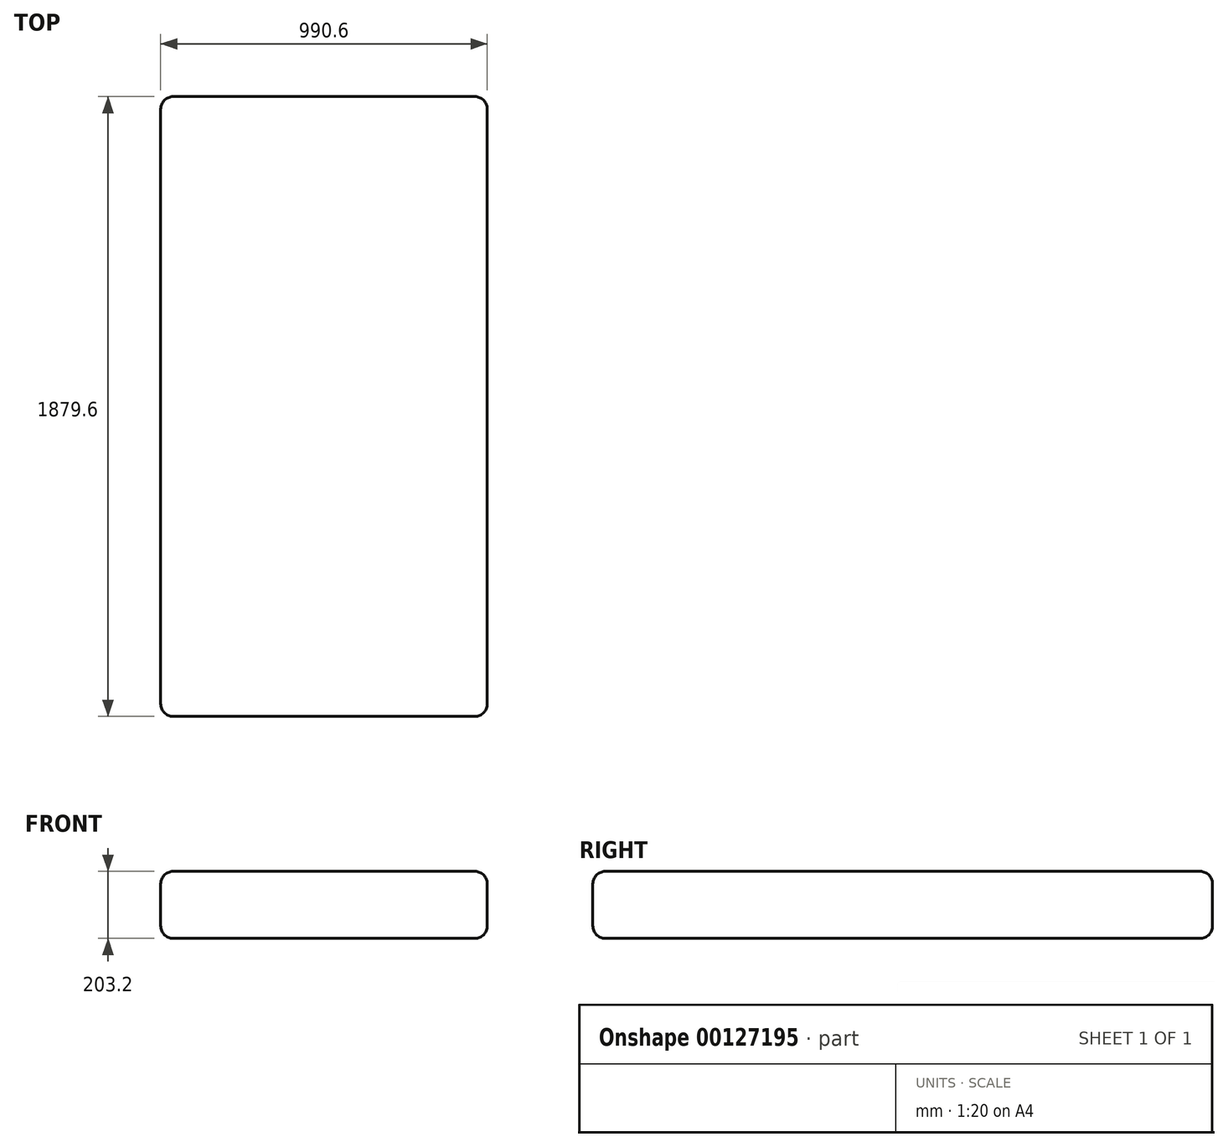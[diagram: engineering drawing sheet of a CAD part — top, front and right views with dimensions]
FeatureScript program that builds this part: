
annotation { "Feature Type Name" : "Feature", "Feature Type Description" : "" }
export const myFeature = defineFeature(function(context is Context, id is Id, definition is map)
    precondition{}
    {
        {
            var Q0;
            Q0=qCreatedBy(makeId("Front.planeOp"),FACE);
            var sketch = newSketch(context, id + "F0", { "sketchPlane" : qUnion([Q0])});
            skLineSegment(sketch, "E0.bottom", {"start": v(457.2, -101.6) * mm, "end": v(-457.2, -101.6) * mm});
            skLineSegment(sketch, "E0.top", {"start": v(457.2, 101.6) * mm, "end": v(-457.2, 101.6) * mm});
            skLineSegment(sketch, "E0.left", {"start": v(495.3, -63.5) * mm, "end": v(495.3, 63.5) * mm});
            skLineSegment(sketch, "E0.right", {"start": v(-495.3, -63.5) * mm, "end": v(-495.3, 63.5) * mm});
            skPoint(sketch, "E0.middle", {"position": v(0, 0) * mm});
            skPoint(sketch, "E1.visualSharp", {"position": v(-495.3, 101.6) * mm});
            skArc(sketch, "E1.filletArc", {"start": v(-457.2, 101.6) * mm, "mid": v(-484.14, 90.44) * mm, "end": v(-495.3, 63.5) * mm});
            skPoint(sketch, "E2.visualSharp", {"position": v(-495.3, -101.6) * mm});
            skArc(sketch, "E2.filletArc", {"start": v(-495.3, -63.5) * mm, "mid": v(-484.14, -90.44) * mm, "end": v(-457.2, -101.6) * mm});
            skPoint(sketch, "E3.visualSharp", {"position": v(495.3, -101.6) * mm});
            skArc(sketch, "E3.filletArc", {"start": v(457.2, -101.6) * mm, "mid": v(484.14, -90.44) * mm, "end": v(495.3, -63.5) * mm});
            skPoint(sketch, "E4.visualSharp", {"position": v(495.3, 101.6) * mm});
            skArc(sketch, "E4.filletArc", {"start": v(495.3, 63.5) * mm, "mid": v(484.14, 90.44) * mm, "end": v(457.2, 101.6) * mm});
            skSolve(sketch);
        }
        {
            var Q0;
            Q0=qSketchRegion(id+"F0",true);
            extrude(context, id + "F1", {"entities" : qUnion([Q0]), "depth" : 1879.6 * mm});
        }
        {
            var Q0;
            Q0=makeQuery(id+"F1.opExtrude","CAP_EDGE",EDGE,{"disambiguationData":[OSD([sQuery(id+"F0.wireOp",EDGE,"E0.left")])],"isStart":false});
            var Q1;
            Q1=makeQuery(id+"F1.opExtrude","SWEPT_EDGE",EDGE,{"disambiguationData":[OSD([sQuery(id+"F0.wireOp",EDGE,"E0.top"),sQuery(id+"F0.wireOp",EDGE,"E4.filletArc")])]});
            var Q2;
            Q2=makeQuery(id+"F1.opExtrude","CAP_EDGE",EDGE,{"disambiguationData":[OSD([sQuery(id+"F0.wireOp",EDGE,"E0.left")])],"isStart":true});
            fillet(context, id + "F2", {"entities" : qUnion([Q0, Q1, Q2]), "radius" : 38.1 * mm, "tangentPropagation" : true, "allowEdgeOverflow" : false});
        }
    });
